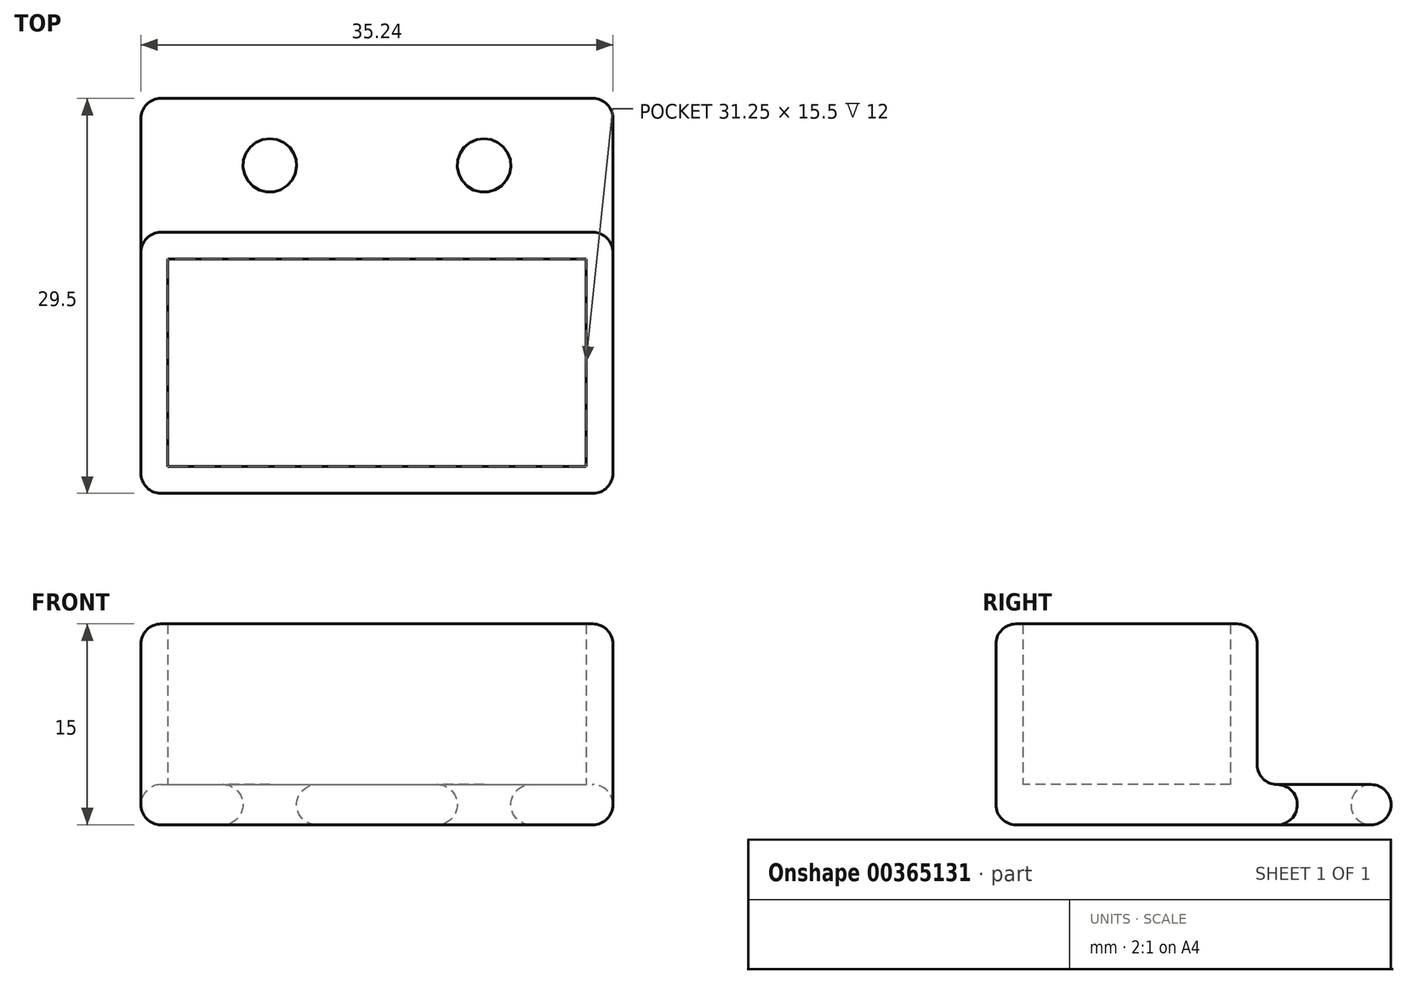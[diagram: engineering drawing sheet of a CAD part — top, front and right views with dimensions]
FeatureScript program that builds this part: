
annotation { "Feature Type Name" : "Feature", "Feature Type Description" : "" }
export const myFeature = defineFeature(function(context is Context, id is Id, definition is map)
    precondition{}
    {
        {
            var Q0;
            Q0=qCreatedBy(makeId("Top.planeOp"),FACE);
            var sketch = newSketch(context, id + "F0", { "sketchPlane" : qUnion([Q0])});
            skLineSegment(sketch, "E0.bottom", {"start": v(-15.62, 7.75) * mm, "end": v(15.62, 7.75) * mm});
            skLineSegment(sketch, "E0.top", {"start": v(-15.62, -7.75) * mm, "end": v(15.62, -7.75) * mm});
            skLineSegment(sketch, "E0.left", {"start": v(-15.62, 7.75) * mm, "end": v(-15.62, -7.75) * mm});
            skLineSegment(sketch, "E0.right", {"start": v(15.62, 7.75) * mm, "end": v(15.62, -7.75) * mm});
            skPoint(sketch, "E0.middle", {"position": v(0, 0) * mm});
            skLineSegment(sketch, "E1.bottom", {"start": v(-17.62, 9.75) * mm, "end": v(17.62, 9.75) * mm});
            skLineSegment(sketch, "E1.top", {"start": v(-17.62, -9.75) * mm, "end": v(17.62, -9.75) * mm});
            skLineSegment(sketch, "E1.left", {"start": v(-17.62, 9.75) * mm, "end": v(-17.62, -9.75) * mm});
            skLineSegment(sketch, "E1.right", {"start": v(17.62, 9.75) * mm, "end": v(17.62, -9.75) * mm});
            skLineSegment(sketch, "E2.top", {"start": v(-17.62, 19.75) * mm, "end": v(17.62, 19.75) * mm});
            skLineSegment(sketch, "E2.left", {"start": v(-17.62, 9.75) * mm, "end": v(-17.62, 19.75) * mm});
            skLineSegment(sketch, "E2.right", {"start": v(17.62, 9.75) * mm, "end": v(17.62, 19.75) * mm});
            skCircle(sketch, "E3", {"center": v(-8, 14.75) * mm, "radius": 2 * mm});
            skCircle(sketch, "E4.1.0.0", {"center": v(8, 14.75) * mm, "radius": 2 * mm});
            skLineSegment(sketch, "E4.direction1", {"start": v(-8, 14.75) * mm, "end": v(8, 14.75) * mm, "construction": true});
            skSolve(sketch);
        }
        {
            var Q0;
            Q0=makeQuery(id+"F0.imprint","IMPRINT",FACE,{"disambiguationData":[TD([[makeQuery(id+"F0.imprint","IMPRINT",EDGE,{"derivedFrom":sQuery(id+"F0.wireOp",EDGE,"E0.bottom")}),1.0]])]});
            extrude(context, id + "F1", {"entities" : qUnion([Q0]), "depth" : 15 * mm});
        }
        {
            var Q0;
            Q0=makeQuery(id+"F0.imprint","IMPRINT",FACE,{"disambiguationData":[TD([[makeQuery(id+"F0.imprint","IMPRINT",EDGE,{"derivedFrom":sQuery(id+"F0.wireOp",EDGE,"E0.bottom")}),-1.0]])]});
            var Q1;
            Q1=makeQuery(id+"F0.imprint","IMPRINT",FACE,{"disambiguationData":[TD([[makeQuery(id+"F0.imprint","IMPRINT",EDGE,{"derivedFrom":sQuery(id+"F0.wireOp",EDGE,"E1.bottom")}),1.0]])]});
            extrude(context, id + "F2", {"entities" : qUnion([Q0, Q1]), "operationType" : NewBodyOperationType.ADD, "depth" : 3 * mm});
        }
        {
            var Q0;
            Q0=makeQuery(id+"F2.opExtrude","CAP_FACE",FACE,{"disambiguationData":[OSD([sQuery(id+"F0.wireOp",EDGE,"E1.bottom"),sQuery(id+"F0.wireOp",EDGE,"E2.top"),sQuery(id+"F0.wireOp",EDGE,"E2.left"),sQuery(id+"F0.wireOp",EDGE,"E2.right"),sQuery(id+"F0.wireOp",EDGE,"E3"),sQuery(id+"F0.wireOp",EDGE,"E4.1.0.0"),sQuery(id+"F0.wireOp",EDGE,"E4.2.0.0"),sQuery(id+"F0.wireOp",EDGE,"E4.3.0.0")])],"isStart":false});
            var Q1;
            {var subQ0=sQuery(id+"F0.wireOp",EDGE,"E1.bottom");var subQ1=sQuery(id+"F0.wireOp",EDGE,"E0.right");var subQ2=sQuery(id+"F0.wireOp",EDGE,"E0.left");var subQ3=sQuery(id+"F0.wireOp",EDGE,"E0.top");var subQ4=sQuery(id+"F0.wireOp",EDGE,"E0.bottom");Q1=makeQuery(id+"F2.boolean.opBoolean","MERGE",FACE,{"derivedFrom":[makeQuery(id+"F1.opExtrude","CAP_FACE",FACE,{"disambiguationData":[OSD([subQ4,subQ3,subQ2,subQ1,sQuery(id+"F0.wireOp",EDGE,"E1.top"),sQuery(id+"F0.wireOp",EDGE,"E1.left"),sQuery(id+"F0.wireOp",EDGE,"E1.right"),subQ0])],"isStart":true}),makeQuery(id+"F2.opExtrude","CAP_FACE",FACE,{"disambiguationData":[OSD([subQ4,subQ3,subQ2,subQ1])],"isStart":true}),makeQuery(id+"F2.opExtrude","CAP_FACE",FACE,{"disambiguationData":[OSD([subQ0,sQuery(id+"F0.wireOp",EDGE,"E2.top"),sQuery(id+"F0.wireOp",EDGE,"E2.left"),sQuery(id+"F0.wireOp",EDGE,"E2.right"),sQuery(id+"F0.wireOp",EDGE,"E3"),sQuery(id+"F0.wireOp",EDGE,"E4.1.0.0"),sQuery(id+"F0.wireOp",EDGE,"E4.2.0.0"),sQuery(id+"F0.wireOp",EDGE,"E4.3.0.0")])],"isStart":true})]});}
            var Q2;
            Q2=makeQuery(id+"F2.boolean.opBoolean","MERGE",FACE,{"derivedFrom":[makeQuery(id+"F1.opExtrude","SWEPT_FACE",FACE,{"disambiguationData":[OSD([sQuery(id+"F0.wireOp",EDGE,"E1.left")])]}),makeQuery(id+"F2.opExtrude","SWEPT_FACE",FACE,{"disambiguationData":[OSD([sQuery(id+"F0.wireOp",EDGE,"E2.left")])]})]});
            var Q3;
            Q3=makeQuery(id+"F2.boolean.opBoolean","MERGE",FACE,{"derivedFrom":[makeQuery(id+"F1.opExtrude","SWEPT_FACE",FACE,{"disambiguationData":[OSD([sQuery(id+"F0.wireOp",EDGE,"E1.right")])]}),makeQuery(id+"F2.opExtrude","SWEPT_FACE",FACE,{"disambiguationData":[OSD([sQuery(id+"F0.wireOp",EDGE,"E2.right")])]})]});
            var Q4;
            Q4=makeQuery(id+"F1.opExtrude","SWEPT_FACE",FACE,{"disambiguationData":[OSD([sQuery(id+"F0.wireOp",EDGE,"E1.top")])]});
            var Q5;
            Q5=makeQuery(id+"F1.opExtrude","SWEPT_FACE",FACE,{"disambiguationData":[OSD([sQuery(id+"F0.wireOp",EDGE,"E1.bottom")])]});
            fillet(context, id + "F3", {"entities" : qUnion([Q0, Q1, Q2, Q3, Q4, Q5]), "radius" : 1.5 * mm, "tangentPropagation" : true, "allowEdgeOverflow" : false});
        }
    });
